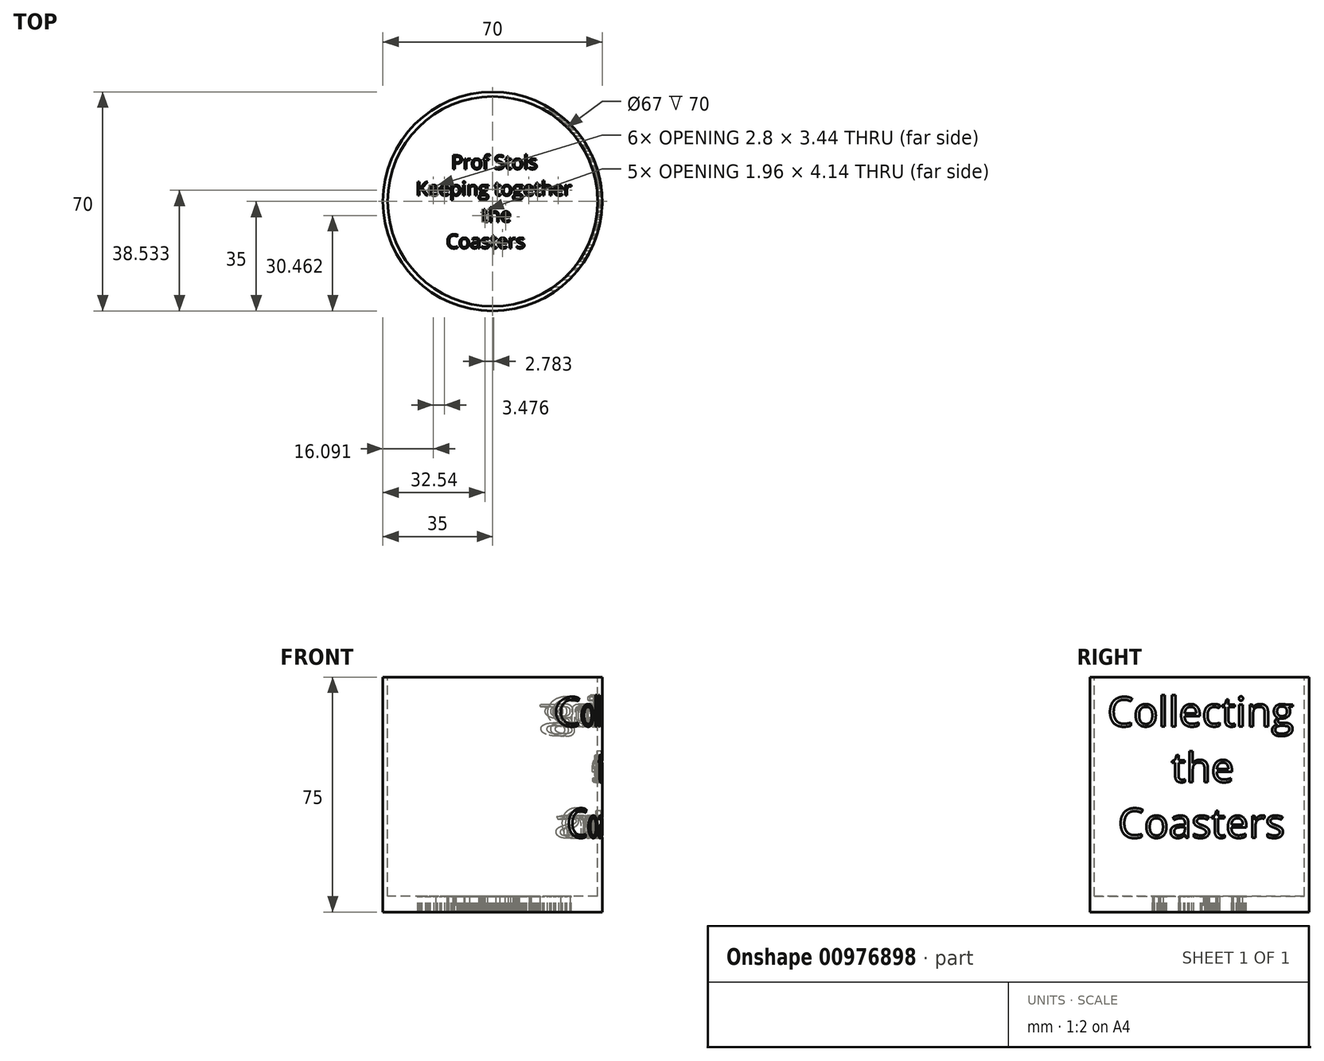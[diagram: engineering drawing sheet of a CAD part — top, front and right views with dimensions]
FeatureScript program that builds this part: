
annotation { "Feature Type Name" : "Feature", "Feature Type Description" : "" }
export const myFeature = defineFeature(function(context is Context, id is Id, definition is map)
    precondition{}
    {
        {
            var Q0;
            Q0=qCreatedBy(makeId("Top.planeOp"),FACE);
            var sketch = newSketch(context, id + "F0", { "sketchPlane" : qUnion([Q0])});
            skCircle(sketch, "E0", {"center": v(0, 0) * mm, "radius": 35 * mm});
            skSolve(sketch);
        }
        {
            var Q0;
            Q0=qSketchRegion(id+"F0",true);
            extrude(context, id + "F1", {"entities" : qUnion([Q0]), "depth" : 75 * mm, "offsetDistance" : 25 * mm});
        }
        {
            var Q0;
            Q0=makeQuery(id+"F1.opExtrude","CAP_FACE",FACE,{"disambiguationData":[OSD([sQuery(id+"F0.wireOp",EDGE,"E0")])],"isStart":false});
            var sketch = newSketch(context, id + "F2", { "sketchPlane" : qUnion([Q0])});
            skCircle(sketch, "E1", {"center": v(0, 0) * mm, "radius": 33.5 * mm});
            skSolve(sketch);
        }
        {
            var Q0;
            Q0=qSketchRegion(id+"F2",true);
            extrude(context, id + "F3", {"entities" : qUnion([Q0]), "operationType" : NewBodyOperationType.REMOVE, "oppositeDirection" : true, "depth" : 70 * mm, "offsetDistance" : 25 * mm});
        }
        {
            var Q0;
            Q0=makeQuery(id+"F3.boolean.opBoolean","COPY",FACE,{"derivedFrom":makeQuery(id+"F3.opExtrude","CAP_FACE",FACE,{"disambiguationData":[OSD([sQuery(id+"F2.wireOp",EDGE,"E1")])],"isStart":false})});
            var sketch = newSketch(context, id + "F4", { "sketchPlane" : qUnion([Q0])});
            skText(sketch, "E2", { "text": "       Prof Stols\nKeeping together\n             the \n      Coasters", "fontName": "OpenSans-Regular.ttf"});
            const initialGuessF4  = {"E2": [-0.02446, 0.0103, 1, 0, 0.00446]};
            skSetInitialGuess(sketch, initialGuessF4);
            skSolve(sketch);
        }
        {
            var Q0;
            Q0=qSketchRegion(id+"F4",true);
            extrude(context, id + "F5", {"entities" : qUnion([Q0]), "operationType" : NewBodyOperationType.REMOVE, "endBound" : BoundingType.THROUGH_ALL, "oppositeDirection" : true, "depth" : 25 * mm, "offsetDistance" : 25 * mm});
        }
        {
            var Q0;
            Q0=qCreatedBy(makeId("Right.planeOp"),FACE);
            var sketch = newSketch(context, id + "F6", { "sketchPlane" : qUnion([Q0])});
            skText(sketch, "E3", { "text": "Collecting \n      the \n Coasters", "fontName": "OpenSans-Regular.ttf"});
            const initialGuessF6  = {"E3": [-0.02934, 0.0593, 1, 0, 0.00942]};
            skSetInitialGuess(sketch, initialGuessF6);
            skSolve(sketch);
        }
        {
            var Q0;
            Q0 = qSketchRegion(id + "F6", true);
            extrude(context, id + "F7", {"entities" : qUnion([Q0]), "operationType" : NewBodyOperationType.REMOVE, "endBound" : BoundingType.THROUGH_ALL, "depth" : 25 * mm, "offsetDistance" : 25 * mm});
        }
    });
